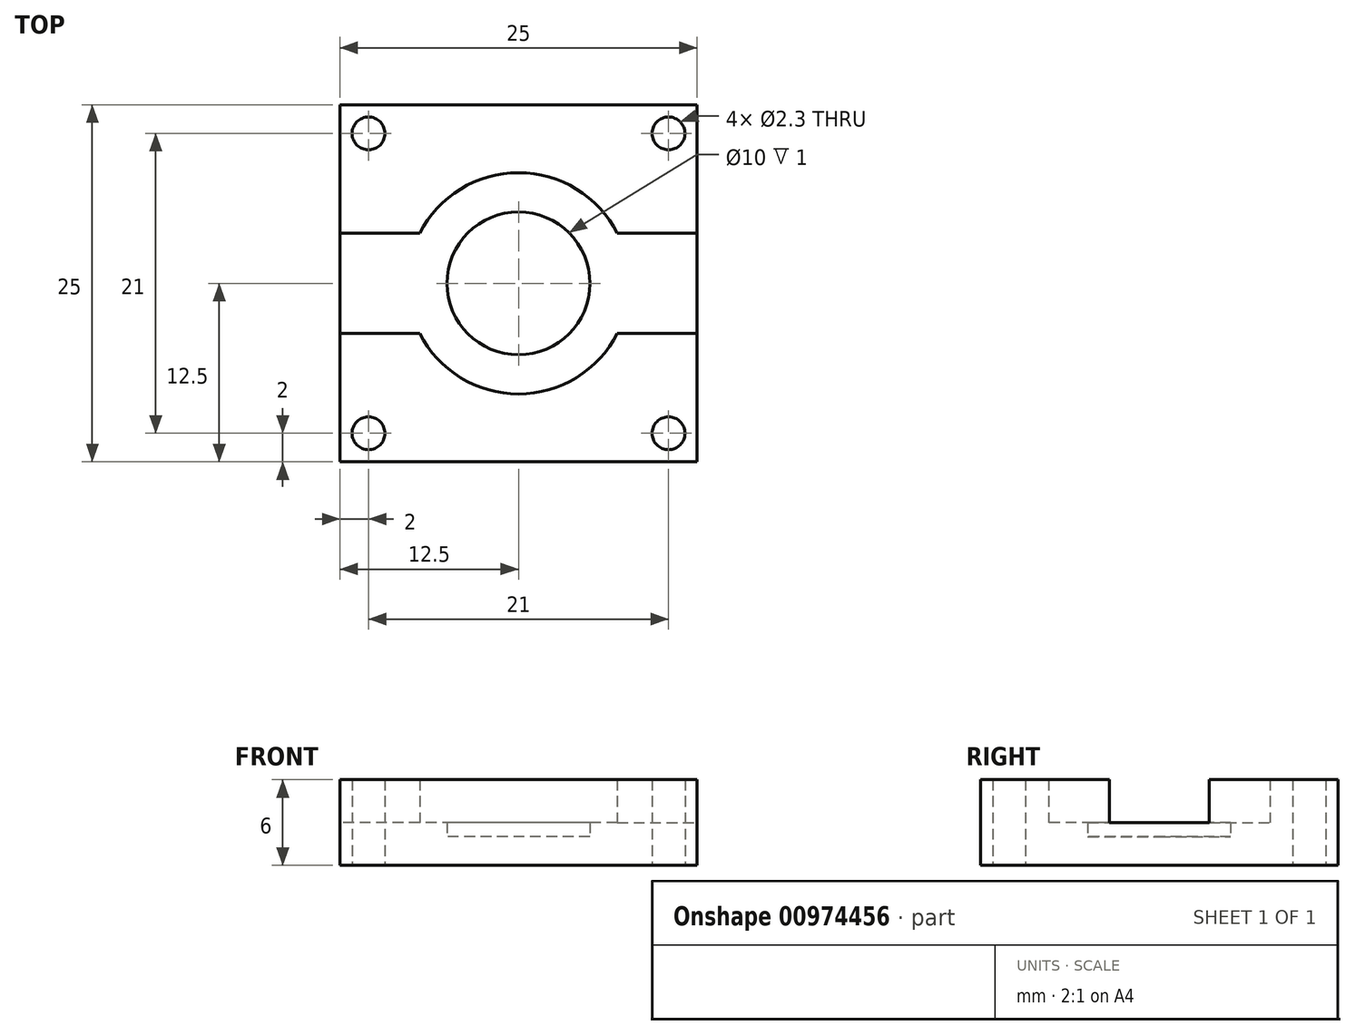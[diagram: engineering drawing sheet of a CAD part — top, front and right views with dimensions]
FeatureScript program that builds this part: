
annotation { "Feature Type Name" : "Feature", "Feature Type Description" : "" }
export const myFeature = defineFeature(function(context is Context, id is Id, definition is map)
    precondition{}
    {
        {
            var Q0;
            Q0=qCreatedBy(makeId("Top.planeOp"),FACE);
            var sketch = newSketch(context, id + "F0", { "sketchPlane" : qUnion([Q0])});
            skCircle(sketch, "E0", {"center": v(0, 0) * mm, "radius": 5 * mm});
            skCircle(sketch, "E1", {"center": v(0, 0) * mm, "radius": 7.75 * mm});
            skLineSegment(sketch, "E2.bottom", {"start": v(-12.5, 12.5) * mm, "end": v(12.5, 12.5) * mm});
            skLineSegment(sketch, "E2.top", {"start": v(-12.5, -12.5) * mm, "end": v(12.5, -12.5) * mm});
            skLineSegment(sketch, "E2.left", {"start": v(-12.5, 12.5) * mm, "end": v(-12.5, -12.5) * mm});
            skLineSegment(sketch, "E2.right", {"start": v(12.5, 12.5) * mm, "end": v(12.5, -12.5) * mm});
            skLineSegment(sketch, "E3", {"start": v(-6.91, 3.5) * mm, "end": v(-12.5, 3.5) * mm});
            skLineSegment(sketch, "E4.MirrorCS", {"start": v(-6.91, -3.5) * mm, "end": v(-12.5, -3.5) * mm});
            skLineSegment(sketch, "E5.MirrorCS", {"start": v(6.91, 3.5) * mm, "end": v(12.5, 3.5) * mm});
            skLineSegment(sketch, "E6.MirrorCS", {"start": v(6.91, -3.5) * mm, "end": v(12.5, -3.5) * mm});
            skLineSegment(sketch, "E7", {"start": v(-12.5, 12.5) * mm, "end": v(12.5, -12.5) * mm, "construction": true});
            skLineSegment(sketch, "E8", {"start": v(12.5, 12.5) * mm, "end": v(-12.5, -12.5) * mm, "construction": true});
            skCircle(sketch, "E9", {"center": v(-10.5, 10.5) * mm, "radius": 1.15 * mm});
            skCircle(sketch, "E10.MirrorC", {"center": v(-10.5, -10.5) * mm, "radius": 1.15 * mm});
            skCircle(sketch, "E11.MirrorC", {"center": v(10.5, 10.5) * mm, "radius": 1.15 * mm});
            skCircle(sketch, "E12.MirrorC", {"center": v(10.5, -10.5) * mm, "radius": 1.15 * mm});
            skSolve(sketch);
        }
        {
            var Q0;
            Q0=makeQuery(id+"F0.imprint","IMPRINT",FACE,{"disambiguationData":[TD([[makeQuery(id+"F0.imprint","IMPRINT",EDGE,{"derivedFrom":sQuery(id+"F0.wireOp",EDGE,"E0")}),-1.0]])]});
            var Q1;
            {var subQ0=sQuery(id+"F0.wireOp",EDGE,"E3");Q1=makeQuery(id+"F0.imprint","IMPRINT",FACE,{"disambiguationData":[TD([[makeQuery(id+"F0.imprint","IMPRINT",EDGE,{"derivedFrom":subQ0}),1.0]])]});}
            var Q2;
            {var subQ0=sQuery(id+"F0.wireOp",EDGE,"E5.MirrorCS");Q2=makeQuery(id+"F0.imprint","IMPRINT",FACE,{"disambiguationData":[TD([[makeQuery(id+"F0.imprint","IMPRINT",EDGE,{"derivedFrom":subQ0}),-1.0]])]});}
            extrude(context, id + "F1", {"entities" : qUnion([Q0, Q1, Q2]), "depth" : 3 * mm, "offsetDistance" : 25 * mm});
        }
        {
            var Q0;
            {var subQ1=sQuery(id+"F0.wireOp",EDGE,"E2.bottom");Q0=makeQuery(id+"F0.imprint","IMPRINT",FACE,{"disambiguationData":[TD([[makeQuery(id+"F0.imprint","IMPRINT",EDGE,{"derivedFrom":subQ1}),-1.0]])]});}
            var Q1;
            {var subQ1=sQuery(id+"F0.wireOp",EDGE,"E2.top");Q1=makeQuery(id+"F0.imprint","IMPRINT",FACE,{"disambiguationData":[TD([[makeQuery(id+"F0.imprint","IMPRINT",EDGE,{"derivedFrom":subQ1}),1.0]])]});}
            extrude(context, id + "F2", {"entities" : qUnion([Q0, Q1]), "operationType" : NewBodyOperationType.ADD, "depth" : 6 * mm, "offsetDistance" : 25 * mm});
        }
        {
            var Q0;
            Q0=makeQuery(id+"F0.imprint","IMPRINT",FACE,{"disambiguationData":[TD([[makeQuery(id+"F0.imprint","IMPRINT",EDGE,{"derivedFrom":sQuery(id+"F0.wireOp",EDGE,"E0")}),1.0]])]});
            extrude(context, id + "F3", {"entities" : qUnion([Q0]), "operationType" : NewBodyOperationType.ADD, "depth" : 2 * mm, "offsetDistance" : 25 * mm});
        }
    });
